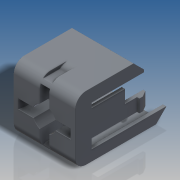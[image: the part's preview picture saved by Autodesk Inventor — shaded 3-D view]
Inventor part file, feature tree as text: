
AUTODESK INVENTOR PART (.ipt)
format: ipt  version: 2016 SP2 (Build 200236200, 236)  size: 641,536 bytes
history: native  units: in
note: dims shown in document units (in); Inventor stores cm internally (conversion verified against a paired STEP export)
features: extrude x11, sketch x6, plane x1, fillet x1, projected_geometry x1
ambient origin geometry x8: Origin, YZ Plane, XZ Plane, XY Plane, X Axis, Y Axis, Z Axis, Center Point
bodies: Solid1 (feature_tree)
feature tree (20):
  sketch  "Sketch2"  dims[d0=0.8504in d1=0.1417in]
  extrude  "Extrusion1"  Depth=0.1417in
  extrude  "Extrusion2"  Depth=0.2205in
  extrude  "Extrusion5"  Depth=0.1417in
  extrude  "Extrusion6"  Depth=0.1732in
  extrude  "Extrusion10"  Depth=0.0315in
  sketch  "Sketch8"  dims[d6=0.1732in d7=0.1732in]
  extrude  "Extrusion11"  Depth=0.0039in
  extrude  "Extrusion14"  Depth=0.0039in
  extrude  "Extrusion12"  Depth=0.0039in
  extrude  "Extrusion13"  Depth=0.0039in
  extrude  "Extrusion15"  Depth=0.0039in
  plane  "Work Plane1"
  extrude  "Extrusion16"  Depth=0.0039in
  fillet  "Fillet1"  Radius=0.5669in
  sketch  "Sketch3"  dims[d2=1.2126in d3=0.2205in]
  projected_geometry  "Projected Loop1"
  sketch  "Sketch7"  dims[d4=45.0deg d5=0.1417in]
  sketch  "Sketch9"  dims[d8=0.1732in d9=0.0315in]
  sketch  "Sketch10"  dims[d10=0.9134in d11=0.063in d12=0.6614in d13=0.8189in d14=0.0567in d15=0.0472in d16=0.063in d21=0.5669in d22=0.8189in d23=0.0in d24=0.7244in d25=0.0in d30=0.315in d31=0.0in d32=0.126in d33=0.0315in d34=0.0472in d35=0.0315in d36=0.315in d37=0.0in d50=0.0039in d61=0.2205in d63=0.2205in d64=0.2362in d65=135.0deg d66=0.063in d67=0.2992in d68=0.0in d69=0.1206in d70=0.315in d71=0.6614in d74=0.0472in d75=0.0472in d76=0.0472in d77=0.315in d78=0.0in d80=0.315in d81=0.0in d82=0.2362in d83=0.315in d84=0.0in d85=0.0875in d86=0.3307in d87=0.0787in d88=0.2362in d89=0.0in d91=0.2362in d92=0.0in d93=0.262in d94=0.378in d95=0.0415in d96=0.0787in d97=0.0157in d98=0.2362in d99=0.0in d100=0.3307in d101=0.0415in]
